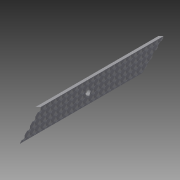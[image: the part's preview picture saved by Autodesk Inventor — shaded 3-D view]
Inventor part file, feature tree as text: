
AUTODESK INVENTOR PART (.ipt)
format: ipt  version: 2015 SP1 (Build 190203100, 203)  size: 378,368 bytes
history: native  units: in
note: dims shown in document units (in); Inventor stores cm internally (conversion verified against a paired STEP export)
features: sketch x3, extrude x2, pattern_linear x1, hole x1
ambient origin geometry x8: Origin, YZ Plane, XZ Plane, XY Plane, X Axis, Y Axis, Z Axis, Center Point
bodies: Solid1 (feature_tree)
feature tree (7):
  extrude  "Extrusion1"  Depth=7.25in
  extrude  "Extrusion2"  Depth=0.125in
  pattern_linear  "Rectangular Pattern1"  Spacing1=0.125in  [1 undecoded]
  hole  "Hole1"  [1 undecoded]
  sketch  "Sketch1"  dims[d0=1.0in d1=7.25in]
  sketch  "Sketch2"  dims[d2=0.125in d3=0.0in d4=0.125in]
  sketch  "Sketch3"  dims[d5=1.0in d6=0.125in d7=1.0in d8=135.0deg d9=45.0deg d10=90.0deg d11=135.0deg d12=90.0deg d13=90.0deg d14=0.0625in d15=-0.4123in d16=11.4173in d18=0.25in d19=0.5in d20=0.5in d21=0.5in d22=3.625in d23=0.5in d24=0.5in d25=0.25in d26=0.75in d27=0.375in d28=0.25in d29=0.5635in d30=1.0in d31=0.8108in]
note: 2 required parameter values undecoded (feature->parameter linkage not recoverable at this tier; creation-order binding heuristic only, values carry confidence <= 0.55)
